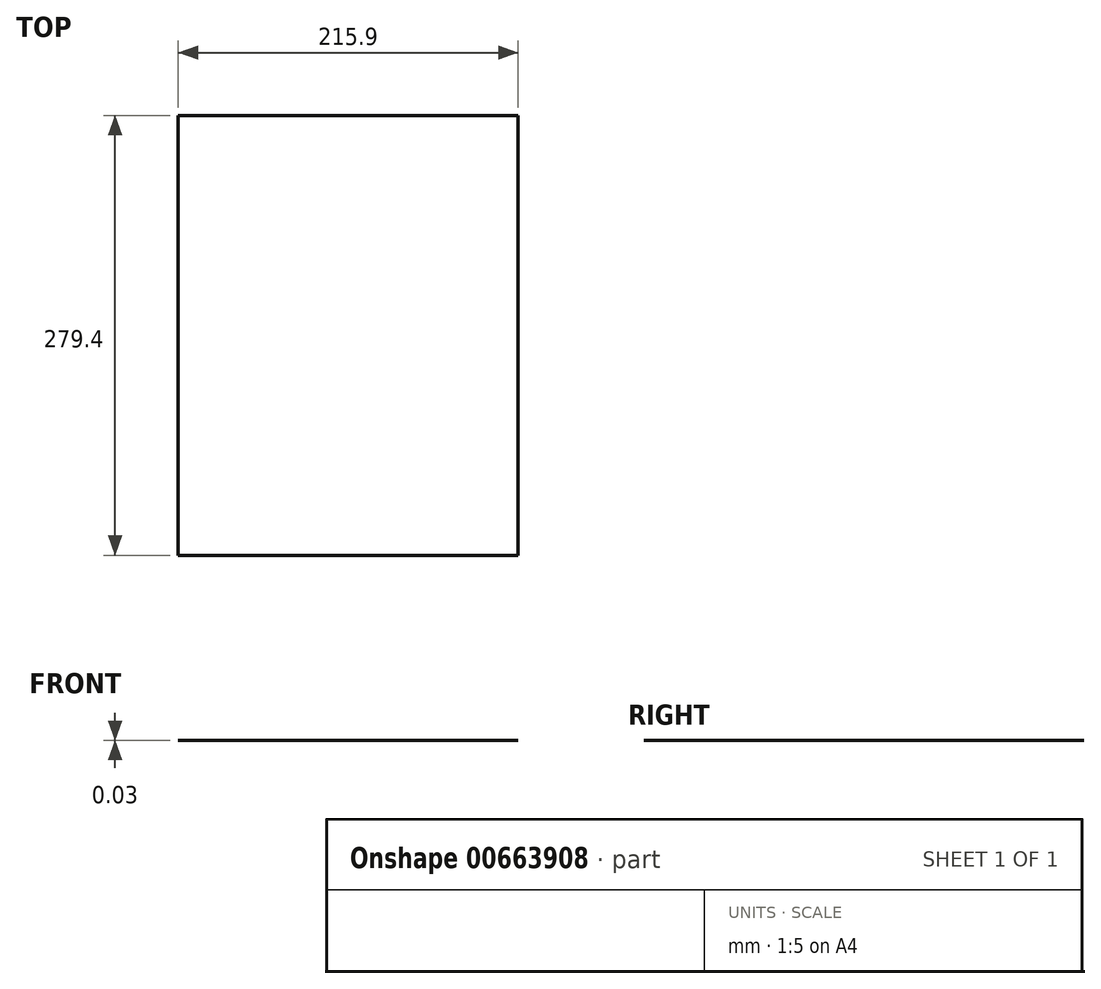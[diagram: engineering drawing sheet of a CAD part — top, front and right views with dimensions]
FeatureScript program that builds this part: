
annotation { "Feature Type Name" : "Feature", "Feature Type Description" : "" }
export const myFeature = defineFeature(function(context is Context, id is Id, definition is map)
    precondition{}
    {
        {
            var Q0;
            Q0=qCreatedBy(makeId("Top.planeOp"),FACE);
            var sketch = newSketch(context, id + "F0", { "sketchPlane" : qUnion([Q0])});
            skLineSegment(sketch, "E0", {"start": v(-47.5, 190.3) * mm, "end": v(-47.5, -89.1) * mm});
            skLineSegment(sketch, "E1", {"start": v(-47.5, -89.1) * mm, "end": v(168.4, -89.1) * mm});
            skLineSegment(sketch, "E2", {"start": v(168.4, -89.1) * mm, "end": v(168.4, 190.3) * mm});
            skLineSegment(sketch, "E3", {"start": v(168.4, 190.3) * mm, "end": v(-47.5, 190.3) * mm});
            skSolve(sketch);
        }
        {
            var Q0;
            Q0 = qSketchRegion(id + "F0", true);
            extrude(context, id + "F1", {"entities" : qUnion([Q0]), "depth" : 0.03 * mm, "offsetDistance" : 25.4 * mm});
        }
    });
